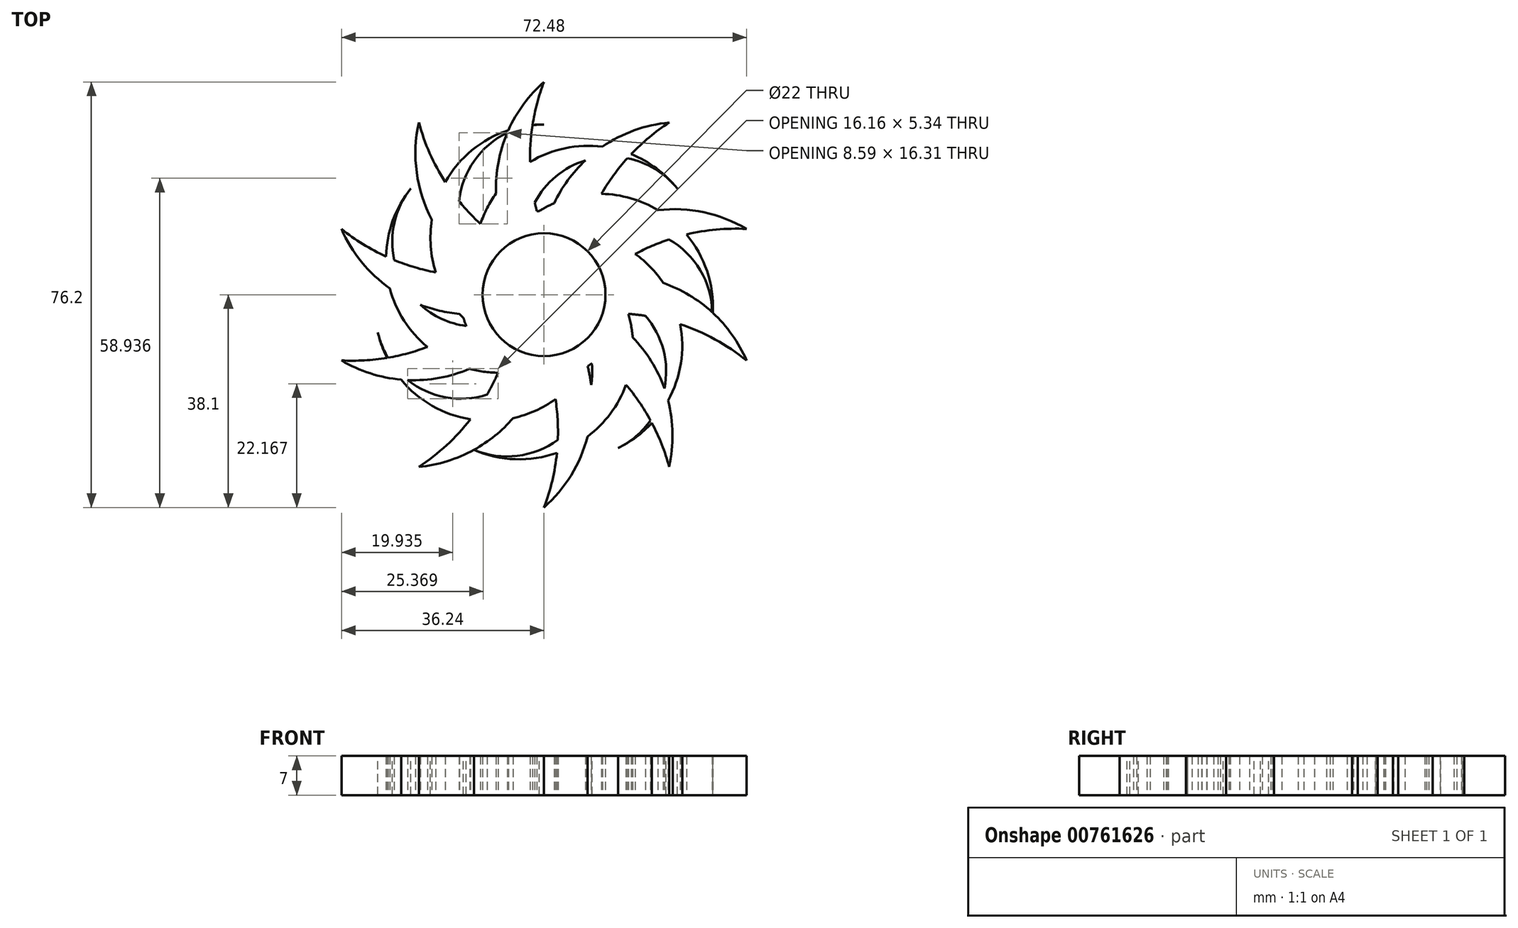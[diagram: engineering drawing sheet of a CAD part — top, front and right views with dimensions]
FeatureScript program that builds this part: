
annotation { "Feature Type Name" : "Feature", "Feature Type Description" : "" }
export const myFeature = defineFeature(function(context is Context, id is Id, definition is map)
    precondition{}
    {
        {
            var Q0;
            Q0=qCreatedBy(makeId("Top.planeOp"),FACE);
            var sketch = newSketch(context, id + "F0", { "sketchPlane" : qUnion([Q0])});
            skCircle(sketch, "E0", {"center": v(0, 0) * mm, "radius": 15 * mm});
            skCircle(sketch, "E1", {"center": v(0, 0) * mm, "radius": 11 * mm});
            skSolve(sketch);
        }
        {
            var Q0;
            Q0=makeQuery(id+"F0.imprint","IMPRINT",FACE,{"disambiguationData":[TD([[makeQuery(id+"F0.imprint","IMPRINT",EDGE,{"derivedFrom":sQuery(id+"F0.wireOp",EDGE,"E0")}),-1.0]])]});
            var Q1;
            Q1=makeQuery(id+"F0.imprint","IMPRINT",FACE,{"disambiguationData":[TD([[makeQuery(id+"F0.imprint","IMPRINT",EDGE,{"derivedFrom":sQuery(id+"F0.wireOp",EDGE,"E0")}),1.0]])]});
            extrude(context, id + "F1", {"entities" : qUnion([Q0, Q1]), "endBound" : BoundingType.SYMMETRIC, "depth" : 7 * mm, "offsetDistance" : 25.4 * mm});
        }
        {
            var Q0;
            Q0=makeQuery(id+"F1.opExtrude","CAP_FACE",FACE,{"disambiguationData":[OSD([sQuery(id+"F0.wireOp",EDGE,"E0"),sQuery(id+"F0.wireOp",EDGE,"E1")])],"isStart":false});
            var sketch = newSketch(context, id + "F2", { "sketchPlane" : qUnion([Q0])});
            skArc(sketch, "E2", {"start": v(0, 30.48) * mm, "mid": v(-13.27, 22.74) * mm, "end": v(-13.06, 7.38) * mm});
            skArc(sketch, "E3", {"start": v(0, 30.48) * mm, "mid": v(-18.76, 17.96) * mm, "end": v(-14.4, -4.17) * mm});
            skCircle(sketch, "E4.0", {"center": v(0, 0) * mm, "radius": 15 * mm});
            skArc(sketch, "E5.1.0", {"start": v(-23.83, 19) * mm, "mid": v(-25.74, -3.47) * mm, "end": v(-5.73, -13.86) * mm});
            skArc(sketch, "E5.1.1", {"start": v(-23.83, 19) * mm, "mid": v(-26.05, 3.8) * mm, "end": v(-13.91, -5.6) * mm});
            skArc(sketch, "E5.2.0", {"start": v(-29.72, -6.78) * mm, "mid": v(-13.34, -22.29) * mm, "end": v(7.27, -13.12) * mm});
            skArc(sketch, "E5.2.1", {"start": v(-29.72, -6.78) * mm, "mid": v(-19.22, -18) * mm, "end": v(-4.3, -14.37) * mm});
            skArc(sketch, "E5.3.0", {"start": v(-13.22, -27.46) * mm, "mid": v(9.11, -24.32) * mm, "end": v(14.8, -2.5) * mm});
            skArc(sketch, "E5.3.1", {"start": v(-13.22, -27.46) * mm, "mid": v(2.09, -26.24) * mm, "end": v(8.56, -12.32) * mm});
            skArc(sketch, "E5.4.0", {"start": v(13.22, -27.46) * mm, "mid": v(24.7, -8.04) * mm, "end": v(11.17, 10) * mm});
            skArc(sketch, "E5.4.1", {"start": v(13.22, -27.46) * mm, "mid": v(21.82, -14.73) * mm, "end": v(14.97, -0.99) * mm});
            skArc(sketch, "E5.5.0", {"start": v(29.72, -6.78) * mm, "mid": v(21.69, 14.3) * mm, "end": v(-0.86, 14.98) * mm});
            skArc(sketch, "E5.5.1", {"start": v(29.72, -6.78) * mm, "mid": v(25.12, 7.87) * mm, "end": v(10.1, 11.09) * mm});
            skArc(sketch, "E5.6.0", {"start": v(23.83, 19) * mm, "mid": v(2.35, 25.87) * mm, "end": v(-12.24, 8.67) * mm});
            skArc(sketch, "E5.6.1", {"start": v(23.83, 19) * mm, "mid": v(9.5, 24.55) * mm, "end": v(-2.37, 14.81) * mm});
            skSolve(sketch);
        }
        {
            var Q0;
            {var subQ0=sQuery(id+"F2.wireOp",EDGE,"b55d5dc6-e6bc-4adf-8808-82faed36b45b.5.0");Q0=makeQuery(id+"F2.imprint","IMPRINT",FACE,{"disambiguationData":[TD([[makeQuery(id+"F2.imprint","IMPRINT",EDGE,{"derivedFrom":subQ0}),1.0]])]});}
            var Q1;
            {var subQ0=sQuery(id+"F2.wireOp",EDGE,"b55d5dc6-e6bc-4adf-8808-82faed36b45b.6.0");Q1=makeQuery(id+"F2.imprint","IMPRINT",FACE,{"disambiguationData":[TD([[makeQuery(id+"F2.imprint","IMPRINT",EDGE,{"derivedFrom":subQ0}),1.0]])]});}
            var Q2;
            {var subQ0=sQuery(id+"F2.wireOp",EDGE,"b55d5dc6-e6bc-4adf-8808-82faed36b45b.7.0");Q2=makeQuery(id+"F2.imprint","IMPRINT",FACE,{"disambiguationData":[TD([[makeQuery(id+"F2.imprint","IMPRINT",EDGE,{"derivedFrom":subQ0}),1.0]])]});}
            var Q3;
            {var subQ0=sQuery(id+"F2.wireOp",EDGE,"E2");Q3=makeQuery(id+"F2.imprint","IMPRINT",FACE,{"disambiguationData":[TD([[makeQuery(id+"F2.imprint","IMPRINT",EDGE,{"derivedFrom":subQ0}),-1.0]])]});}
            var Q4;
            {var subQ0=sQuery(id+"F2.wireOp",EDGE,"b55d5dc6-e6bc-4adf-8808-82faed36b45b.1.0");Q4=makeQuery(id+"F2.imprint","IMPRINT",FACE,{"disambiguationData":[TD([[makeQuery(id+"F2.imprint","IMPRINT",EDGE,{"derivedFrom":subQ0}),1.0]])]});}
            var Q5;
            {var subQ0=sQuery(id+"F2.wireOp",EDGE,"b55d5dc6-e6bc-4adf-8808-82faed36b45b.2.0");Q5=makeQuery(id+"F2.imprint","IMPRINT",FACE,{"disambiguationData":[TD([[makeQuery(id+"F2.imprint","IMPRINT",EDGE,{"derivedFrom":subQ0}),1.0]])]});}
            var Q6;
            {var subQ0=sQuery(id+"F2.wireOp",EDGE,"b55d5dc6-e6bc-4adf-8808-82faed36b45b.3.0");Q6=makeQuery(id+"F2.imprint","IMPRINT",FACE,{"disambiguationData":[TD([[makeQuery(id+"F2.imprint","IMPRINT",EDGE,{"derivedFrom":subQ0}),1.0]])]});}
            var Q7;
            {var subQ0=sQuery(id+"F2.wireOp",EDGE,"b55d5dc6-e6bc-4adf-8808-82faed36b45b.4.0");Q7=makeQuery(id+"F2.imprint","IMPRINT",FACE,{"disambiguationData":[TD([[makeQuery(id+"F2.imprint","IMPRINT",EDGE,{"derivedFrom":subQ0}),1.0]])]});}
            var Q8;
            {var subQ0=sQuery(id+"F2.wireOp",EDGE,"E5.6.0");Q8=makeQuery(id+"F2.imprint","IMPRINT",FACE,{"disambiguationData":[TD([[makeQuery(id+"F2.imprint","IMPRINT",EDGE,{"derivedFrom":subQ0}),1.0]])]});}
            var Q9;
            {var subQ0=sQuery(id+"F2.wireOp",EDGE,"E5.5.0");Q9=makeQuery(id+"F2.imprint","IMPRINT",FACE,{"disambiguationData":[TD([[makeQuery(id+"F2.imprint","IMPRINT",EDGE,{"derivedFrom":subQ0}),1.0]])]});}
            var Q10;
            {var subQ0=sQuery(id+"F2.wireOp",EDGE,"E5.4.0");Q10=makeQuery(id+"F2.imprint","IMPRINT",FACE,{"disambiguationData":[TD([[makeQuery(id+"F2.imprint","IMPRINT",EDGE,{"derivedFrom":subQ0}),1.0]])]});}
            var Q11;
            {var subQ0=sQuery(id+"F2.wireOp",EDGE,"E5.3.0");Q11=makeQuery(id+"F2.imprint","IMPRINT",FACE,{"disambiguationData":[TD([[makeQuery(id+"F2.imprint","IMPRINT",EDGE,{"derivedFrom":subQ0}),1.0]])]});}
            var Q12;
            {var subQ0=sQuery(id+"F2.wireOp",EDGE,"E5.2.0");Q12=makeQuery(id+"F2.imprint","IMPRINT",FACE,{"disambiguationData":[TD([[makeQuery(id+"F2.imprint","IMPRINT",EDGE,{"derivedFrom":subQ0}),1.0]])]});}
            var Q13;
            {var subQ0=sQuery(id+"F2.wireOp",EDGE,"E5.1.0");Q13=makeQuery(id+"F2.imprint","IMPRINT",FACE,{"disambiguationData":[TD([[makeQuery(id+"F2.imprint","IMPRINT",EDGE,{"derivedFrom":subQ0}),1.0]])]});}
            extrude(context, id + "F3", {"entities" : qUnion([Q0, Q1, Q2, Q3, Q4, Q5, Q6, Q7, Q8, Q9, Q10, Q11, Q12, Q13]), "operationType" : NewBodyOperationType.ADD, "oppositeDirection" : true, "depth" : 7 * mm, "offsetDistance" : 25.4 * mm});
        }
        {
            var Q0;
            Q0=qCreatedBy(makeId("Top.planeOp"),FACE);
            var sketch = newSketch(context, id + "F4", { "sketchPlane" : qUnion([Q0])});
            skPoint(sketch, "E6.visualSharp", {"position": v(0, 38.1) * mm});
            skArc(sketch, "E7", {"start": v(0, 38.1) * mm, "mid": v(-8, 24.55) * mm, "end": v(-6.48, 8.89) * mm});
            skArc(sketch, "E8.1.0", {"start": v(-22.4, 30.82) * mm, "mid": v(-20.9, 15.16) * mm, "end": v(-10.47, 3.38) * mm});
            skArc(sketch, "E8.2.0", {"start": v(-36.24, 11.77) * mm, "mid": v(-25.82, -0.02) * mm, "end": v(-10.46, -3.41) * mm});
            skArc(sketch, "E8.3.0", {"start": v(-36.24, -11.77) * mm, "mid": v(-20.88, -15.2) * mm, "end": v(-6.45, -8.9) * mm});
            skArc(sketch, "E8.4.0", {"start": v(-22.4, -30.82) * mm, "mid": v(-7.96, -24.56) * mm, "end": v(0.02, -11) * mm});
            skArc(sketch, "E8.5.0", {"start": v(0, -38.1) * mm, "mid": v(8, -24.55) * mm, "end": v(6.48, -8.89) * mm});
            skArc(sketch, "E8.6.0", {"start": v(22.4, -30.82) * mm, "mid": v(20.9, -15.16) * mm, "end": v(10.47, -3.38) * mm});
            skArc(sketch, "E8.7.0", {"start": v(36.24, -11.77) * mm, "mid": v(25.82, 0.02) * mm, "end": v(10.46, 3.41) * mm});
            skArc(sketch, "E8.8.0", {"start": v(36.24, 11.77) * mm, "mid": v(20.88, 15.2) * mm, "end": v(6.45, 8.9) * mm});
            skArc(sketch, "E8.9.0", {"start": v(22.4, 30.82) * mm, "mid": v(7.96, 24.56) * mm, "end": v(-0.02, 11) * mm});
            skPoint(sketch, "E8.center", {"position": v(0, 0) * mm});
            skCircle(sketch, "E9", {"center": v(0, 0) * mm, "radius": 11 * mm});
            skArc(sketch, "E10", {"start": v(0, 38.1) * mm, "mid": v(-2.5, 24.55) * mm, "end": v(-0.02, 11) * mm});
            skArc(sketch, "E11.1.0", {"start": v(-22.4, 30.82) * mm, "mid": v(-16.45, 18.4) * mm, "end": v(-6.48, 8.89) * mm});
            skArc(sketch, "E11.2.0", {"start": v(-36.24, 11.77) * mm, "mid": v(-24.12, 5.21) * mm, "end": v(-10.47, 3.38) * mm});
            skArc(sketch, "E11.3.0", {"start": v(-36.24, -11.77) * mm, "mid": v(-22.58, -9.96) * mm, "end": v(-10.46, -3.41) * mm});
            skArc(sketch, "E11.4.0", {"start": v(-22.4, -30.82) * mm, "mid": v(-12.4, -21.33) * mm, "end": v(-6.45, -8.9) * mm});
            skArc(sketch, "E11.5.0", {"start": v(0, -38.1) * mm, "mid": v(2.5, -24.55) * mm, "end": v(0.02, -11) * mm});
            skArc(sketch, "E11.6.0", {"start": v(22.4, -30.82) * mm, "mid": v(16.45, -18.4) * mm, "end": v(6.48, -8.89) * mm});
            skArc(sketch, "E11.7.0", {"start": v(36.24, -11.77) * mm, "mid": v(24.12, -5.21) * mm, "end": v(10.47, -3.38) * mm});
            skArc(sketch, "E11.8.0", {"start": v(36.24, 11.77) * mm, "mid": v(22.58, 9.96) * mm, "end": v(10.46, 3.41) * mm});
            skArc(sketch, "E11.9.0", {"start": v(22.4, 30.82) * mm, "mid": v(12.4, 21.33) * mm, "end": v(6.45, 8.9) * mm});
            skSolve(sketch);
        }
        {
            var Q0;
            {var subQ0=sQuery(id+"F4.wireOp",EDGE,"E8.1.0");Q0=makeQuery(id+"F4.imprint","IMPRINT",FACE,{"disambiguationData":[TD([[makeQuery(id+"F4.imprint","IMPRINT",EDGE,{"derivedFrom":subQ0}),1.0]])]});}
            var Q1;
            {var subQ0=sQuery(id+"F4.wireOp",EDGE,"E7");Q1=makeQuery(id+"F4.imprint","IMPRINT",FACE,{"disambiguationData":[TD([[makeQuery(id+"F4.imprint","IMPRINT",EDGE,{"derivedFrom":subQ0}),1.0]])]});}
            var Q2;
            {var subQ0=sQuery(id+"F4.wireOp",EDGE,"E8.9.0");Q2=makeQuery(id+"F4.imprint","IMPRINT",FACE,{"disambiguationData":[TD([[makeQuery(id+"F4.imprint","IMPRINT",EDGE,{"derivedFrom":subQ0}),1.0]])]});}
            var Q3;
            {var subQ0=sQuery(id+"F4.wireOp",EDGE,"E8.8.0");Q3=makeQuery(id+"F4.imprint","IMPRINT",FACE,{"disambiguationData":[TD([[makeQuery(id+"F4.imprint","IMPRINT",EDGE,{"derivedFrom":subQ0}),1.0]])]});}
            var Q4;
            {var subQ0=sQuery(id+"F4.wireOp",EDGE,"E8.7.0");Q4=makeQuery(id+"F4.imprint","IMPRINT",FACE,{"disambiguationData":[TD([[makeQuery(id+"F4.imprint","IMPRINT",EDGE,{"derivedFrom":subQ0}),1.0]])]});}
            var Q5;
            {var subQ0=sQuery(id+"F4.wireOp",EDGE,"E8.6.0");Q5=makeQuery(id+"F4.imprint","IMPRINT",FACE,{"disambiguationData":[TD([[makeQuery(id+"F4.imprint","IMPRINT",EDGE,{"derivedFrom":subQ0}),1.0]])]});}
            var Q6;
            {var subQ0=sQuery(id+"F4.wireOp",EDGE,"E8.5.0");Q6=makeQuery(id+"F4.imprint","IMPRINT",FACE,{"disambiguationData":[TD([[makeQuery(id+"F4.imprint","IMPRINT",EDGE,{"derivedFrom":subQ0}),1.0]])]});}
            var Q7;
            {var subQ0=sQuery(id+"F4.wireOp",EDGE,"E8.4.0");Q7=makeQuery(id+"F4.imprint","IMPRINT",FACE,{"disambiguationData":[TD([[makeQuery(id+"F4.imprint","IMPRINT",EDGE,{"derivedFrom":subQ0}),1.0]])]});}
            var Q8;
            {var subQ0=sQuery(id+"F4.wireOp",EDGE,"E8.3.0");Q8=makeQuery(id+"F4.imprint","IMPRINT",FACE,{"disambiguationData":[TD([[makeQuery(id+"F4.imprint","IMPRINT",EDGE,{"derivedFrom":subQ0}),1.0]])]});}
            var Q9;
            {var subQ0=sQuery(id+"F4.wireOp",EDGE,"E8.2.0");Q9=makeQuery(id+"F4.imprint","IMPRINT",FACE,{"disambiguationData":[TD([[makeQuery(id+"F4.imprint","IMPRINT",EDGE,{"derivedFrom":subQ0}),1.0]])]});}
            extrude(context, id + "F5", {"entities" : qUnion([Q0, Q1, Q2, Q3, Q4, Q5, Q6, Q7, Q8, Q9]), "operationType" : NewBodyOperationType.ADD, "endBound" : BoundingType.SYMMETRIC, "depth" : 7 * mm, "offsetDistance" : 25.4 * mm});
        }
    });
